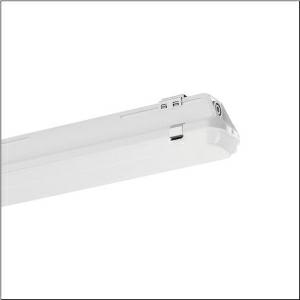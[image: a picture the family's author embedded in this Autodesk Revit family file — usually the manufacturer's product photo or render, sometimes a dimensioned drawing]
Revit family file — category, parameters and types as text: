
# Revit family: monsun_r__11_51fp207p430h_33e7
name_source: partatom
category: Lighting Fixtures
units: mm (PartAtom-declared; Revit-internal decimal feet)

## family parameters
Cut with Voids When Loaded = No
Host = Face
Light Source = No
Part Type = Normal
Room Calculation Point = No
Round Connector Dimension = Use Diameter
Shared = No

## types (1)
- Monsun® 11 (1 x LED, 3990 lm, 24.8 W, 4000K)
    Apparent Load = 25 VA
    CIE Flux Codes = 45 75 93 94 100
    Color Rendering = 80
    Color Temperature = 4000K
    Default Elevation = 1800 mm
    Description = Monsun® 11, damp-proof luminaire, chain hanger, primary optical cover: enclosure, of PC, light emission: direct distribution, primary light characteristic: symmetric, installation type: suspended mounting, surface-mounted, horizontal mounting, vertical mounting, LED, rated luminous flux: 3.990lm, luminous efficacy: 161lm/W, light colour: 840, colour temperature: 4000K, control gear: ON/OFF, with terminal, 3-pole, max. 2.5mm², mains connection: 220..240V, AC, 50/60Hz, rated input power: 25W, luminaire housing, of glass-fibre reinforced polyester, uncoated, bright grey, incl. chain hanger, length: 1.590mm, width: 90mm, height: 88mm, clip for enclosure, of stainless steel (V2A), ceiling mounting element, of stainless steel (V2A), chain hanger, of stainless steel (V2A), protection rating (complete): IP66, insulation class (complete): insulation class I (protective earthing), certification: CE, ENEC, VDE, UKCA, protection symbol: D, impact resistance: IK08, permissible operating ambient temperature: -35..+40°C, standard: EN 50419, EN 60598-2-1, no direct snow, no direct sun, no direct rain, for indoor or canopied outdoor use, corresponds to IFS (International Featured Standards) requirements for safety and quality in the food industry, contact your sales advisor before using the luminaires in applications with unclear chemical exposure, large temperature fluctuations or condensation-forming humidity, LABS conformity tested according to VDMA 24364:2018-05, packaging unit: 1 piece
    Height = 89 mm
    Lamp = 1 x LED
    Lamp Light Flux = 3990 lm
    Lamp Power = 24.8 W
    Lamp count = 1
    Length = 1590 mm
    Luminous efficacy = 161 lm/W
    Manufacturer = Siteco
    ModVariant = No
    Model = 51FP207P430H
    Mounting Place = Ceiling
    Mounting Type = Surface mounted
    Number of Poles = 1
    OnlyDefault = Yes
    Power Factor = 1
    Product Name = Monsun® 11
    Product group = damp-proof luminaire
    ProductGroupID = 301
    Protection Class = Protection class I
    Protection Degree = IP 66
    RLX_Detail_Level = 1
    RLX_Emergency_Light_Flux = 0 lm
    RLX_Emergency_Type = 0
    RLX_Emergency_Type_DB = No
    RlxData = <blob elided: 88897 chars, md5=eb6423dc>
    Socket = socket
    Standby Power = 0 W
    System Light Flux = 3990 lm
    System Power = 25 W
    Type Comments = Product without accessories
    Type Image = l_1349237.jpg
    URL = http://relux.com
    VarID = ---
    Voltage = 0 V
    Weight = 0.00 kg
    Width = 90 mm

## geometry (parser evidence)
native form markers: Blend x4, Sweep x12
no freeform markers — native parametric forms only
